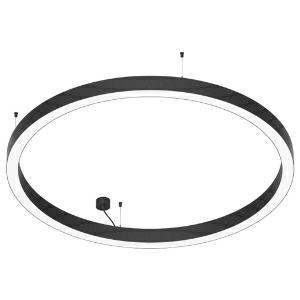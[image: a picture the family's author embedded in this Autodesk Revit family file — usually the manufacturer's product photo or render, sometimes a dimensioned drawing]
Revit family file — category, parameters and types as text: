
# Revit family: glorious_slim_410-9642
name_source: partatom
category: Leuchten
revit_build: Autodesk Revit 2016 (Build: 20190508_0715(x64)
units: mm (PartAtom-declared; Revit-internal decimal feet)

## family parameters
Basisbauteil = Fläche
Beim Laden mit Abzugskörper schneiden = Nein
Bemaßung runder Anschluss = Durchmesser verwenden
Gemeinsam genutzt = Nein
Lichtquelle = Nein
Raumberechnungspunkt = Nein
Teiletyp = Normal

## types (1)
- 410-9642-D01-H27 (4 x LED, 405.68 lm, 3.1 W, 2700K)
    Beschreibung = GLORIOUS SLIM
    CIE Flux Codes = 48 79 96 100 78
    Color Rendering = 1A/90…99
    Color Temperature = 2700K
    Height = 90 mm
    Hersteller = Prolicht
    Lamp Light Flux = 405.68 lm
    Lamp Power = 3.1 W
    Lamp count = 4
    Lampe = 4 x LED
    Length = 583 mm
    Luminous efficacy = 103 lm/W
    ModVariant = Nein
    Modell = 410-9642
    Mounting Place = Ceiling
    Mounting Type = Pendant
    Number of Poles = 1
    OnlyDefault = Ja
    Power Factor = 1
    Product Name = GLORIOUS SLIM
    Product group = Suspended lights
    ProductGroupID = 941
    Protection Class = Protection class
    Protection Degree = Degree of protection
    RLX_Detail_Level = 1
    RlxData = <blob elided: 58073 chars, md5=af3e513d>
    Scheinlast = 198 VA
    Socket = socket
    Standby Power = 0 W
    System Light Flux = 20355 lm
    System Power = 198 W
    Typenbild = 410-9642.jpg
    Typenkommentare = DIFFUSER Opal (01),LED COLOUR DIR 2700 K (27)
    URL = http://relux.com
    VarID = 410-9642-d01-h27
    Voltage = 0 V
    Vorgabe-Ansicht = 1800 mm
    Weight = 0.00 kg
    Width = 65 mm

## geometry (parser evidence)
native form markers: Blend x4, Sweep x52
no freeform markers — native parametric forms only
